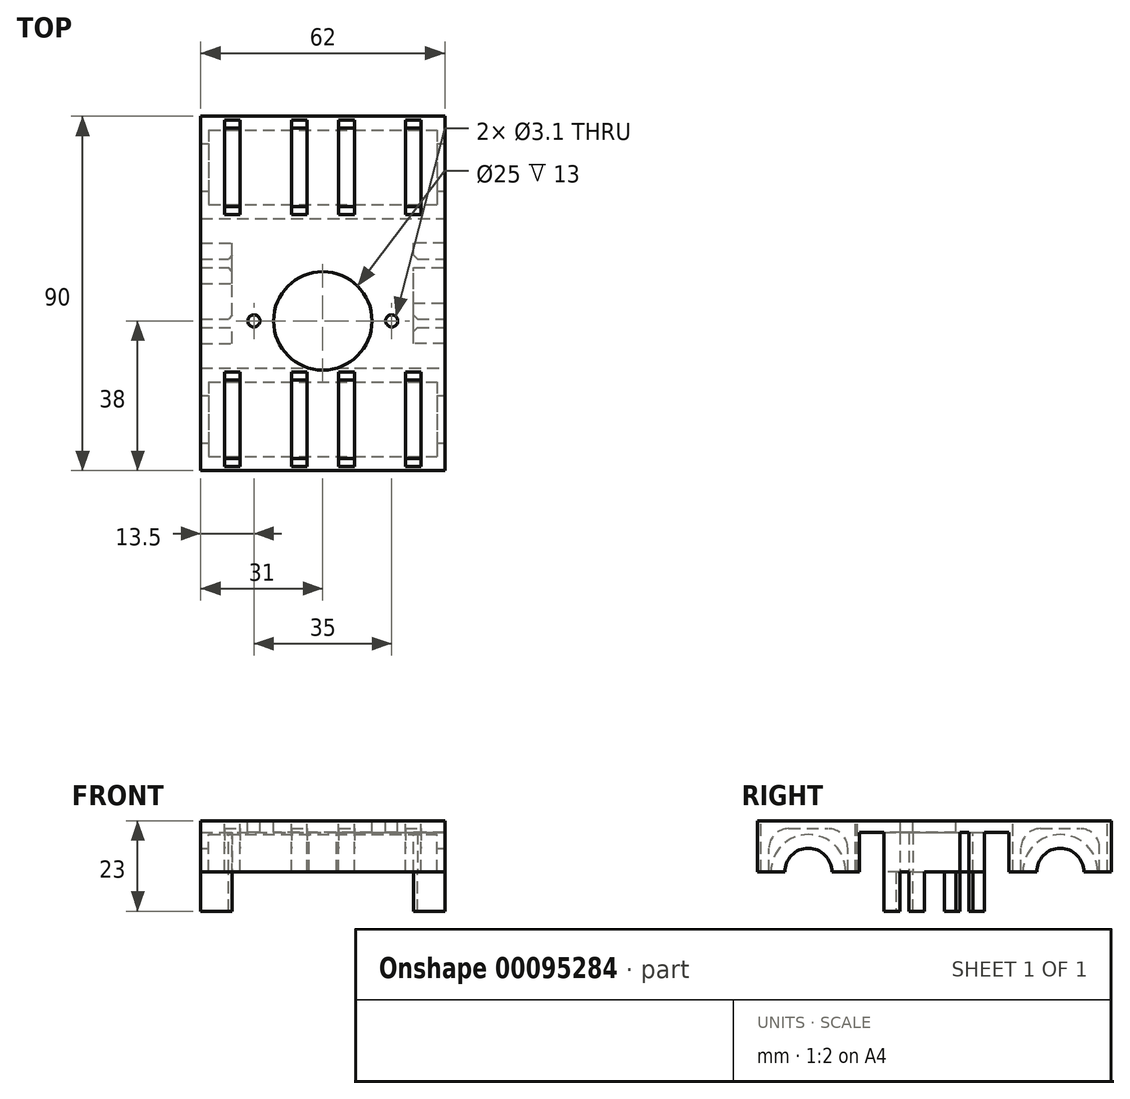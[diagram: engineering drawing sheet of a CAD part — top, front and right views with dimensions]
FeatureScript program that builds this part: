
annotation { "Feature Type Name" : "Feature", "Feature Type Description" : "" }
export const myFeature = defineFeature(function(context is Context, id is Id, definition is map)
    precondition{}
    {
        {
            var Q0;
            Q0=qCreatedBy(makeId("Top.planeOp"),FACE);
            var sketch = newSketch(context, id + "F0", { "sketchPlane" : qUnion([Q0])});
            skLineSegment(sketch, "E0.bottom", {"start": v(31, 45) * mm, "end": v(-31, 45) * mm});
            skLineSegment(sketch, "E0.top", {"start": v(31, -45) * mm, "end": v(-31, -45) * mm});
            skLineSegment(sketch, "E0.left", {"start": v(31, 45) * mm, "end": v(31, -45) * mm});
            skLineSegment(sketch, "E0.right", {"start": v(-31, 45) * mm, "end": v(-31, -45) * mm});
            skPoint(sketch, "E0.middle", {"position": v(0, 0) * mm});
            skLineSegment(sketch, "E1.bottom", {"start": v(-29, -22.5) * mm, "end": v(0, -22.5) * mm, "construction": true});
            skLineSegment(sketch, "E1.top", {"start": v(-29, -41.5) * mm, "end": v(0, -41.5) * mm, "construction": true});
            skLineSegment(sketch, "E1.left", {"start": v(-29, -22.5) * mm, "end": v(-29, -41.5) * mm, "construction": true});
            skLineSegment(sketch, "E1.right", {"start": v(0, -22.5) * mm, "end": v(0, -41.5) * mm});
            skLineSegment(sketch, "E2.bottom", {"start": v(0, -22.5) * mm, "end": v(29, -22.5) * mm, "construction": true});
            skLineSegment(sketch, "E2.top", {"start": v(0, -41.5) * mm, "end": v(29, -41.5) * mm, "construction": true});
            skLineSegment(sketch, "E2.left", {"start": v(0, -22.5) * mm, "end": v(0, -41.5) * mm, "construction": true});
            skLineSegment(sketch, "E2.right", {"start": v(29, -22.5) * mm, "end": v(29, -41.5) * mm, "construction": true});
            skLineSegment(sketch, "E3.MirrorCS", {"start": v(-29, 22.5) * mm, "end": v(0, 22.5) * mm, "construction": true});
            skLineSegment(sketch, "E4.MirrorCS", {"start": v(-29, 22.5) * mm, "end": v(-29, 41.5) * mm, "construction": true});
            skLineSegment(sketch, "E5.MirrorCS", {"start": v(-29, 41.5) * mm, "end": v(0, 41.5) * mm, "construction": true});
            skLineSegment(sketch, "E6.MirrorCS", {"start": v(0, 41.5) * mm, "end": v(29, 41.5) * mm, "construction": true});
            skLineSegment(sketch, "E7.MirrorCS", {"start": v(0, 22.5) * mm, "end": v(0, 41.5) * mm, "construction": true});
            skLineSegment(sketch, "E8.MirrorCS", {"start": v(0, 22.5) * mm, "end": v(29, 22.5) * mm, "construction": true});
            skLineSegment(sketch, "E9.MirrorCS", {"start": v(29, 22.5) * mm, "end": v(29, 41.5) * mm, "construction": true});
            skPoint(sketch, "E10", {"position": v(0, 32) * mm});
            skPoint(sketch, "E11", {"position": v(0, -32) * mm});
            skLineSegment(sketch, "E12.bottom", {"start": v(38, -27) * mm, "end": v(-38, -27) * mm, "construction": true});
            skLineSegment(sketch, "E12.top", {"start": v(38, -37) * mm, "end": v(-38, -37) * mm, "construction": true});
            skLineSegment(sketch, "E12.left", {"start": v(38, -27) * mm, "end": v(38, -37) * mm, "construction": true});
            skLineSegment(sketch, "E12.right", {"start": v(-38, -27) * mm, "end": v(-38, -37) * mm, "construction": true});
            skSolve(sketch);
        }
        {
            var Q0;
            Q0 = qSketchRegion(id + "F0", true);
            extrude(context, id + "F1", {"entities" : qUnion([Q0]), "depth" : 3 * mm});
        }
        {
            var Q0;
            Q0=makeQuery(id+"F1.opExtrude","CAP_FACE",FACE,{"disambiguationData":[OSD([sQuery(id+"F0.wireOp",EDGE,"E0.bottom"),sQuery(id+"F0.wireOp",EDGE,"E0.top"),sQuery(id+"F0.wireOp",EDGE,"E0.left"),sQuery(id+"F0.wireOp",EDGE,"E0.right"),sQuery(id+"F0.wireOp",EDGE,"JYYRxy27-rgmN-2rHz-wlqE-8sxhEuyDvCgZ"),sQuery(id+"F0.wireOp",EDGE,"MYyJY7mb-jWNP-WgpS-Wrbd-b0EtJ2tdOFdo"),sQuery(id+"F0.wireOp",EDGE,"f8288d83-7b8a-4c9c-ad61-19536bc560240.MirrorC")])],"isStart":true});
            var sketch = newSketch(context, id + "F2", { "sketchPlane" : qUnion([Q0])});
            skLineSegment(sketch, "E13.bottom", {"start": v(-31, 45) * mm, "end": v(31, 45) * mm});
            skLineSegment(sketch, "E13.top", {"start": v(-31, 19) * mm, "end": v(31, 19) * mm});
            skLineSegment(sketch, "E13.left", {"start": v(-31, 45) * mm, "end": v(-31, 19) * mm});
            skLineSegment(sketch, "E13.right", {"start": v(31, 45) * mm, "end": v(31, 19) * mm});
            skLineSegment(sketch, "E14", {"start": v(-31, 32) * mm, "end": v(31, 32) * mm, "construction": true});
            skLineSegment(sketch, "E15.MirrorCS", {"start": v(-31, -32) * mm, "end": v(31, -32) * mm, "construction": true});
            skLineSegment(sketch, "E16.MirrorCS", {"start": v(31, -45) * mm, "end": v(31, -19) * mm});
            skLineSegment(sketch, "E17.MirrorCS", {"start": v(-31, -45) * mm, "end": v(-31, -19) * mm});
            skLineSegment(sketch, "E18.MirrorCS", {"start": v(-31, -19) * mm, "end": v(31, -19) * mm});
            skLineSegment(sketch, "E19.MirrorCS", {"start": v(-31, -45) * mm, "end": v(31, -45) * mm});
            skSolve(sketch);
        }
        {
            var Q0;
            Q0 = qSketchRegion(id + "F2", true);
            extrude(context, id + "F3", {"entities" : qUnion([Q0]), "operationType" : NewBodyOperationType.ADD, "depth" : (20 / 2) * mm});
        }
        {
            var Q0;
            Q0=qCreatedBy(makeId("Right.planeOp"),FACE);
            var sketch = newSketch(context, id + "F4", { "sketchPlane" : qUnion([Q0])});
            skCircle(sketch, "E20", {"center": v(-32, -10) * mm, "radius": 9.5 * mm});
            skCircle(sketch, "E21.MirrorC", {"center": v(32, -10) * mm, "radius": 9.5 * mm});
            skSolve(sketch);
        }
        {
            var Q0;
            Q0 = qSketchRegion(id + "F4", true);
            var Q1;
            Q1=sQuery(id+"F4.wireOp",EDGE,"E20");
            extrude(context, id + "F5", {"entities" : qUnion([Q0]), "operationType" : NewBodyOperationType.REMOVE, "surfaceEntities" : qUnion([Q1]), "endBound" : BoundingType.SYMMETRIC, "oppositeDirection" : true, "depth" : (29 * 2) * mm});
        }
        {
            var Q0;
            Q0=qCreatedBy(makeId("Right.planeOp"),FACE);
            var sketch = newSketch(context, id + "F6", { "sketchPlane" : qUnion([Q0])});
            skCircle(sketch, "E22", {"center": v(-32, -10) * mm, "radius": 6 * mm});
            skCircle(sketch, "E23.MirrorC", {"center": v(32, -10) * mm, "radius": 6 * mm});
            skSolve(sketch);
        }
        {
            var Q0;
            Q0 = qSketchRegion(id + "F6", true);
            extrude(context, id + "F7", {"entities" : qUnion([Q0]), "operationType" : NewBodyOperationType.REMOVE, "endBound" : BoundingType.THROUGH_ALL, "oppositeDirection" : true, "depth" : 25 * mm, "hasSecondDirection" : true, "secondDirectionBound" : SecondDirectionBoundingType.THROUGH_ALL, "secondDirectionOppositeDirection" : false, "secondDirectionDepth" : 25 * mm});
        }
        {
            var Q0;
            Q0=makeQuery(id+"F1.opExtrude","CAP_FACE",FACE,{"disambiguationData":[OSD([sQuery(id+"F0.wireOp",EDGE,"E0.bottom"),sQuery(id+"F0.wireOp",EDGE,"E0.top"),sQuery(id+"F0.wireOp",EDGE,"E0.left"),sQuery(id+"F0.wireOp",EDGE,"E0.right"),sQuery(id+"F0.wireOp",EDGE,"MYyJY7mb-jWNP-WgpS-Wrbd-b0EtJ2tdOFdo"),sQuery(id+"F0.wireOp",EDGE,"f8288d83-7b8a-4c9c-ad61-19536bc560240.MirrorC")])],"isStart":false});
            var sketch = newSketch(context, id + "F8", { "sketchPlane" : qUnion([Q0])});
            skLineSegment(sketch, "E24.bottom", {"start": v(-29, -22.5) * mm, "end": v(0, -22.5) * mm, "construction": true});
            skLineSegment(sketch, "E24.top", {"start": v(-29, -41.5) * mm, "end": v(0, -41.5) * mm, "construction": true});
            skLineSegment(sketch, "E24.left", {"start": v(-29, -22.5) * mm, "end": v(-29, -41.5) * mm, "construction": true});
            skLineSegment(sketch, "E25.bottom", {"start": v(0, -22.5) * mm, "end": v(29, -22.5) * mm, "construction": true});
            skLineSegment(sketch, "E25.top", {"start": v(0, -41.5) * mm, "end": v(29, -41.5) * mm, "construction": true});
            skLineSegment(sketch, "E25.left", {"start": v(0, -22.5) * mm, "end": v(0, -41.5) * mm, "construction": true});
            skLineSegment(sketch, "E25.right", {"start": v(29, -22.5) * mm, "end": v(29, -41.5) * mm, "construction": true});
            skCircle(sketch, "E26", {"center": v(0, -7) * mm, "radius": 12.5 * mm});
            skCircle(sketch, "E27", {"center": v(-17.5, -7) * mm, "radius": 1.55 * mm});
            skPoint(sketch, "E28", {"position": v(0, -32) * mm});
            skCircle(sketch, "E29.MirrorC", {"center": v(17.5, -7) * mm, "radius": 1.55 * mm});
            skLineSegment(sketch, "E30", {"start": v(-38.23, -32) * mm, "end": v(52.87, -32) * mm, "construction": true});
            skLineSegment(sketch, "E31.MirrorCS", {"start": v(-29, 41.5) * mm, "end": v(0, 41.5) * mm, "construction": true});
            skLineSegment(sketch, "E32.MirrorCS", {"start": v(0, 41.5) * mm, "end": v(29, 41.5) * mm, "construction": true});
            skLineSegment(sketch, "E33.MirrorCS", {"start": v(29, 22.5) * mm, "end": v(29, 41.5) * mm, "construction": true});
            skLineSegment(sketch, "E34.MirrorCS", {"start": v(0, 22.5) * mm, "end": v(29, 22.5) * mm, "construction": true});
            skLineSegment(sketch, "E35.MirrorCS", {"start": v(0, 22.5) * mm, "end": v(0, 41.5) * mm, "construction": true});
            skLineSegment(sketch, "E36.MirrorCS", {"start": v(-38.23, 32) * mm, "end": v(52.87, 32) * mm, "construction": true});
            skLineSegment(sketch, "E37.MirrorCS", {"start": v(-29, 22.5) * mm, "end": v(0, 22.5) * mm, "construction": true});
            skLineSegment(sketch, "E38.MirrorCS", {"start": v(-29, 22.5) * mm, "end": v(-29, 41.5) * mm, "construction": true});
            skSolve(sketch);
        }
        {
            var Q0;
            Q0 = qSketchRegion(id + "F8", true);
            extrude(context, id + "F9", {"entities" : qUnion([Q0]), "operationType" : NewBodyOperationType.REMOVE, "endBound" : BoundingType.THROUGH_ALL, "oppositeDirection" : true, "depth" : 25 * mm});
        }
        {
            var Q0;
            Q0=qCreatedBy(makeId("Right.planeOp"),FACE);
            cPlane(context, id + "F10", {"entities" : qUnion([Q0]), "cplaneType" : CPlaneType.OFFSET, "offset" : (29 - 6) * mm, "width" : 150 * mm, "height" : 150 * mm});
        }
        {
            var Q0;
            Q0=qCreatedBy(id+"F10.planeOp",FACE);
            var sketch = newSketch(context, id + "F11", { "sketchPlane" : qUnion([Q0])});
            skLineSegment(sketch, "E39.bottom", {"start": v(-44, -10) * mm, "end": v(-42, -10) * mm});
            skLineSegment(sketch, "E39.top", {"start": v(-44, 3) * mm, "end": v(-20, 3) * mm});
            skLineSegment(sketch, "E39.left", {"start": v(-44, -10) * mm, "end": v(-44, 3) * mm});
            skLineSegment(sketch, "E39.right", {"start": v(-20, -10) * mm, "end": v(-20, 3) * mm});
            skLineSegment(sketch, "E40.top", {"start": v(-37, 1) * mm, "end": v(-27, 1) * mm});
            skLineSegment(sketch, "E40.left", {"start": v(-42, -10) * mm, "end": v(-42, -4) * mm});
            skLineSegment(sketch, "E40.right", {"start": v(-22, -10) * mm, "end": v(-22, -4) * mm});
            skLineSegment(sketch, "E41.trimOffspring", {"start": v(-22, -10) * mm, "end": v(-20, -10) * mm});
            skPoint(sketch, "E42.visualSharp", {"position": v(-42, 1) * mm});
            skArc(sketch, "E42.filletArc", {"start": v(-37, 1) * mm, "mid": v(-40.54, -0.46) * mm, "end": v(-42, -4) * mm});
            skPoint(sketch, "E43.visualSharp", {"position": v(-22, 1) * mm});
            skArc(sketch, "E43.filletArc", {"start": v(-22, -4) * mm, "mid": v(-23.46, -0.46) * mm, "end": v(-27, 1) * mm});
            skLineSegment(sketch, "E44", {"start": v(-32, -18.67) * mm, "end": v(-32, 4.8) * mm, "construction": true});
            skPoint(sketch, "E45", {"position": v(-32, -10) * mm});
            skPoint(sketch, "E46", {"position": v(-32, 1) * mm});
            skLineSegment(sketch, "E47.MirrorCS", {"start": v(-20, -10) * mm, "end": v(-22, -10) * mm});
            skLineSegment(sketch, "E48.MirrorCS", {"start": v(-20, 3) * mm, "end": v(-44, 3) * mm});
            skArc(sketch, "E49.MirrorCS", {"start": v(-27, 1) * mm, "mid": v(-23.46, -0.46) * mm, "end": v(-22, -4) * mm});
            skArc(sketch, "E50.MirrorCS", {"start": v(-42, -4) * mm, "mid": v(-40.54, -0.46) * mm, "end": v(-37, 1) * mm});
            skLineSegment(sketch, "E51.MirrorCS", {"start": v(-42, -10) * mm, "end": v(-44, -10) * mm});
            skLineSegment(sketch, "E52.MirrorCS", {"start": v(-27, 1) * mm, "end": v(-37, 1) * mm});
            skPoint(sketch, "E53.MirrorP", {"position": v(32, -10) * mm});
            skPoint(sketch, "E54.MirrorP", {"position": v(22, 1) * mm});
            skLineSegment(sketch, "E55.MirrorCS", {"start": v(42, -10) * mm, "end": v(42, -4) * mm});
            skLineSegment(sketch, "E56.MirrorCS", {"start": v(20, -10) * mm, "end": v(20, 3) * mm});
            skLineSegment(sketch, "E57.MirrorCS", {"start": v(44, -10) * mm, "end": v(44, 3) * mm});
            skLineSegment(sketch, "E58.MirrorCS", {"start": v(37, 1) * mm, "end": v(27, 1) * mm});
            skLineSegment(sketch, "E59.MirrorCS", {"start": v(42, -10) * mm, "end": v(44, -10) * mm});
            skLineSegment(sketch, "E60.MirrorCS", {"start": v(22, -10) * mm, "end": v(22, -4) * mm});
            skArc(sketch, "E61.MirrorCS", {"start": v(27, 1) * mm, "mid": v(23.46, -0.46) * mm, "end": v(22, -4) * mm});
            skArc(sketch, "E62.MirrorCS", {"start": v(37, 1) * mm, "mid": v(40.54, -0.46) * mm, "end": v(42, -4) * mm});
            skLineSegment(sketch, "E63.MirrorCS", {"start": v(20, 3) * mm, "end": v(44, 3) * mm});
            skLineSegment(sketch, "E64.MirrorCS", {"start": v(20, -10) * mm, "end": v(22, -10) * mm});
            skPoint(sketch, "E65.MirrorP", {"position": v(42, 1) * mm});
            skPoint(sketch, "E66.MirrorP", {"position": v(32, 1) * mm});
            skArc(sketch, "E67.MirrorCS", {"start": v(42, -4) * mm, "mid": v(40.54, -0.46) * mm, "end": v(37, 1) * mm});
            skArc(sketch, "E68.MirrorCS", {"start": v(22, -4) * mm, "mid": v(23.46, -0.46) * mm, "end": v(27, 1) * mm});
            skLineSegment(sketch, "E69.MirrorCS", {"start": v(44, 3) * mm, "end": v(20, 3) * mm});
            skLineSegment(sketch, "E70.MirrorCS", {"start": v(44, -10) * mm, "end": v(42, -10) * mm});
            skLineSegment(sketch, "E71.MirrorCS", {"start": v(32, -18.67) * mm, "end": v(32, 4.8) * mm, "construction": true});
            skLineSegment(sketch, "E72.MirrorCS", {"start": v(27, 1) * mm, "end": v(37, 1) * mm});
            skLineSegment(sketch, "E73.MirrorCS", {"start": v(22, -10) * mm, "end": v(20, -10) * mm});
            skSolve(sketch);
        }
        {
            var Q0;
            Q0=qCreatedBy(makeId("Right.planeOp"),FACE);
            cPlane(context, id + "F12", {"entities" : qUnion([Q0]), "cplaneType" : CPlaneType.OFFSET, "offset" : 6 * mm, "width" : 150 * mm, "height" : 150 * mm});
        }
        {
            var Q0;
            Q0=qCreatedBy(id+"F12.planeOp",FACE);
            var sketch = newSketch(context, id + "F13", { "sketchPlane" : qUnion([Q0])});
            skLineSegment(sketch, "E74.bottom", {"start": v(-44, -10) * mm, "end": v(-42, -10) * mm});
            skLineSegment(sketch, "E74.top", {"start": v(-44, 3) * mm, "end": v(-20, 3) * mm});
            skLineSegment(sketch, "E74.left", {"start": v(-44, -10) * mm, "end": v(-44, 3) * mm});
            skLineSegment(sketch, "E74.right", {"start": v(-20, -10) * mm, "end": v(-20, 3) * mm});
            skLineSegment(sketch, "E75.top", {"start": v(-37, 1) * mm, "end": v(-27, 1) * mm});
            skLineSegment(sketch, "E75.left", {"start": v(-42, -10) * mm, "end": v(-42, -4) * mm});
            skLineSegment(sketch, "E75.right", {"start": v(-22, -10) * mm, "end": v(-22, -4) * mm});
            skLineSegment(sketch, "E76.trimOffspring", {"start": v(-22, -10) * mm, "end": v(-20, -10) * mm});
            skPoint(sketch, "E77.visualSharp", {"position": v(-42, 1) * mm});
            skArc(sketch, "E77.filletArc", {"start": v(-37, 1) * mm, "mid": v(-40.54, -0.46) * mm, "end": v(-42, -4) * mm});
            skPoint(sketch, "E78.visualSharp", {"position": v(-22, 1) * mm});
            skArc(sketch, "E78.filletArc", {"start": v(-22, -4) * mm, "mid": v(-23.46, -0.46) * mm, "end": v(-27, 1) * mm});
            skLineSegment(sketch, "E79", {"start": v(-32, -15.28) * mm, "end": v(-32, 8.2) * mm, "construction": true});
            skPoint(sketch, "E80", {"position": v(-32, -10) * mm});
            skPoint(sketch, "E81", {"position": v(-32, 1) * mm});
            skLineSegment(sketch, "E82.MirrorCS", {"start": v(-20, -10) * mm, "end": v(-22, -10) * mm});
            skLineSegment(sketch, "E83.MirrorCS", {"start": v(-20, 3) * mm, "end": v(-44, 3) * mm});
            skArc(sketch, "E84.MirrorCS", {"start": v(-27, 1) * mm, "mid": v(-23.46, -0.46) * mm, "end": v(-22, -4) * mm});
            skArc(sketch, "E85.MirrorCS", {"start": v(-42, -4) * mm, "mid": v(-40.54, -0.46) * mm, "end": v(-37, 1) * mm});
            skLineSegment(sketch, "E86.MirrorCS", {"start": v(-42, -10) * mm, "end": v(-44, -10) * mm});
            skLineSegment(sketch, "E87.MirrorCS", {"start": v(-27, 1) * mm, "end": v(-37, 1) * mm});
            skLineSegment(sketch, "E88.MirrorCS", {"start": v(22, -10) * mm, "end": v(20, -10) * mm});
            skLineSegment(sketch, "E89.MirrorCS", {"start": v(44, -10) * mm, "end": v(42, -10) * mm});
            skPoint(sketch, "E90.MirrorP", {"position": v(32, -10) * mm});
            skLineSegment(sketch, "E91.MirrorCS", {"start": v(20, -10) * mm, "end": v(20, 3) * mm});
            skLineSegment(sketch, "E92.MirrorCS", {"start": v(44, -10) * mm, "end": v(44, 3) * mm});
            skArc(sketch, "E93.MirrorCS", {"start": v(37, 1) * mm, "mid": v(40.54, -0.46) * mm, "end": v(42, -4) * mm});
            skLineSegment(sketch, "E94.MirrorCS", {"start": v(44, 3) * mm, "end": v(20, 3) * mm});
            skPoint(sketch, "E95.MirrorP", {"position": v(22, 1) * mm});
            skLineSegment(sketch, "E96.MirrorCS", {"start": v(42, -10) * mm, "end": v(42, -4) * mm});
            skLineSegment(sketch, "E97.MirrorCS", {"start": v(37, 1) * mm, "end": v(27, 1) * mm});
            skPoint(sketch, "E98.MirrorP", {"position": v(32, 1) * mm});
            skLineSegment(sketch, "E99.MirrorCS", {"start": v(22, -10) * mm, "end": v(22, -4) * mm});
            skArc(sketch, "E100.MirrorCS", {"start": v(27, 1) * mm, "mid": v(23.46, -0.46) * mm, "end": v(22, -4) * mm});
            skPoint(sketch, "E101.MirrorP", {"position": v(42, 1) * mm});
            skLineSegment(sketch, "E102.MirrorCS", {"start": v(42, -10) * mm, "end": v(44, -10) * mm});
            skLineSegment(sketch, "E103.MirrorCS", {"start": v(20, 3) * mm, "end": v(44, 3) * mm});
            skArc(sketch, "E104.MirrorCS", {"start": v(22, -4) * mm, "mid": v(23.46, -0.46) * mm, "end": v(27, 1) * mm});
            skArc(sketch, "E105.MirrorCS", {"start": v(42, -4) * mm, "mid": v(40.54, -0.46) * mm, "end": v(37, 1) * mm});
            skLineSegment(sketch, "E106.MirrorCS", {"start": v(27, 1) * mm, "end": v(37, 1) * mm});
            skLineSegment(sketch, "E107.MirrorCS", {"start": v(20, -10) * mm, "end": v(22, -10) * mm});
            skLineSegment(sketch, "E108.MirrorCS", {"start": v(32, -15.28) * mm, "end": v(32, 8.2) * mm, "construction": true});
            skSolve(sketch);
        }
        {
            var Q0;
            Q0=qCreatedBy(makeId("Right.planeOp"),FACE);
            cPlane(context, id + "F14", {"entities" : qUnion([Q0]), "cplaneType" : CPlaneType.OFFSET, "offset" : (29 - 6) * mm, "oppositeDirection" : true, "width" : 150 * mm, "height" : 150 * mm});
        }
        {
            var Q0;
            Q0=qCreatedBy(id+"F14.planeOp",FACE);
            var sketch = newSketch(context, id + "F15", { "sketchPlane" : qUnion([Q0])});
            skLineSegment(sketch, "E109.bottom", {"start": v(-44, -10) * mm, "end": v(-42, -10) * mm});
            skLineSegment(sketch, "E109.top", {"start": v(-44, 3) * mm, "end": v(-20, 3) * mm});
            skLineSegment(sketch, "E109.left", {"start": v(-44, -10) * mm, "end": v(-44, 3) * mm});
            skLineSegment(sketch, "E109.right", {"start": v(-20, -10) * mm, "end": v(-20, 3) * mm});
            skLineSegment(sketch, "E110.top", {"start": v(-37, 1) * mm, "end": v(-27, 1) * mm});
            skLineSegment(sketch, "E110.left", {"start": v(-42, -10) * mm, "end": v(-42, -4) * mm});
            skLineSegment(sketch, "E110.right", {"start": v(-22, -10) * mm, "end": v(-22, -4) * mm});
            skLineSegment(sketch, "E111.trimOffspring", {"start": v(-22, -10) * mm, "end": v(-20, -10) * mm});
            skPoint(sketch, "E112.visualSharp", {"position": v(-42, 1) * mm});
            skArc(sketch, "E112.filletArc", {"start": v(-37, 1) * mm, "mid": v(-40.54, -0.46) * mm, "end": v(-42, -4) * mm});
            skPoint(sketch, "E113.visualSharp", {"position": v(-22, 1) * mm});
            skArc(sketch, "E113.filletArc", {"start": v(-22, -4) * mm, "mid": v(-23.46, -0.46) * mm, "end": v(-27, 1) * mm});
            skLineSegment(sketch, "E114", {"start": v(-32, -15.28) * mm, "end": v(-32, 8.2) * mm, "construction": true});
            skPoint(sketch, "E115", {"position": v(-32, -10) * mm});
            skPoint(sketch, "E116", {"position": v(-32, 1) * mm});
            skLineSegment(sketch, "E117.MirrorCS", {"start": v(-20, -10) * mm, "end": v(-22, -10) * mm});
            skLineSegment(sketch, "E118.MirrorCS", {"start": v(-20, 3) * mm, "end": v(-44, 3) * mm});
            skArc(sketch, "E119.MirrorCS", {"start": v(-27, 1) * mm, "mid": v(-23.46, -0.46) * mm, "end": v(-22, -4) * mm});
            skArc(sketch, "E120.MirrorCS", {"start": v(-42, -4) * mm, "mid": v(-40.54, -0.46) * mm, "end": v(-37, 1) * mm});
            skLineSegment(sketch, "E121.MirrorCS", {"start": v(-42, -10) * mm, "end": v(-44, -10) * mm});
            skLineSegment(sketch, "E122.MirrorCS", {"start": v(-27, 1) * mm, "end": v(-37, 1) * mm});
            skLineSegment(sketch, "E123.MirrorCS", {"start": v(44, -10) * mm, "end": v(42, -10) * mm});
            skLineSegment(sketch, "E124.MirrorCS", {"start": v(22, -10) * mm, "end": v(22, -4) * mm});
            skLineSegment(sketch, "E125.MirrorCS", {"start": v(44, -10) * mm, "end": v(44, 3) * mm});
            skLineSegment(sketch, "E126.MirrorCS", {"start": v(20, -10) * mm, "end": v(22, -10) * mm});
            skArc(sketch, "E127.MirrorCS", {"start": v(27, 1) * mm, "mid": v(23.46, -0.46) * mm, "end": v(22, -4) * mm});
            skPoint(sketch, "E128.MirrorP", {"position": v(32, 1) * mm});
            skLineSegment(sketch, "E129.MirrorCS", {"start": v(20, -10) * mm, "end": v(20, 3) * mm});
            skPoint(sketch, "E130.MirrorP", {"position": v(42, 1) * mm});
            skLineSegment(sketch, "E131.MirrorCS", {"start": v(27, 1) * mm, "end": v(37, 1) * mm});
            skPoint(sketch, "E132.MirrorP", {"position": v(32, -10) * mm});
            skArc(sketch, "E133.MirrorCS", {"start": v(37, 1) * mm, "mid": v(40.54, -0.46) * mm, "end": v(42, -4) * mm});
            skLineSegment(sketch, "E134.MirrorCS", {"start": v(42, -10) * mm, "end": v(42, -4) * mm});
            skLineSegment(sketch, "E135.MirrorCS", {"start": v(20, 3) * mm, "end": v(44, 3) * mm});
            skPoint(sketch, "E136.MirrorP", {"position": v(22, 1) * mm});
            skLineSegment(sketch, "E137.MirrorCS", {"start": v(37, 1) * mm, "end": v(27, 1) * mm});
            skLineSegment(sketch, "E138.MirrorCS", {"start": v(22, -10) * mm, "end": v(20, -10) * mm});
            skLineSegment(sketch, "E139.MirrorCS", {"start": v(32, -15.28) * mm, "end": v(32, 8.2) * mm, "construction": true});
            skLineSegment(sketch, "E140.MirrorCS", {"start": v(44, 3) * mm, "end": v(20, 3) * mm});
            skArc(sketch, "E141.MirrorCS", {"start": v(22, -4) * mm, "mid": v(23.46, -0.46) * mm, "end": v(27, 1) * mm});
            skArc(sketch, "E142.MirrorCS", {"start": v(42, -4) * mm, "mid": v(40.54, -0.46) * mm, "end": v(37, 1) * mm});
            skLineSegment(sketch, "E143.MirrorCS", {"start": v(42, -10) * mm, "end": v(44, -10) * mm});
            skSolve(sketch);
        }
        {
            var Q0;
            Q0=qCreatedBy(makeId("Right.planeOp"),FACE);
            cPlane(context, id + "F16", {"entities" : qUnion([Q0]), "cplaneType" : CPlaneType.OFFSET, "offset" : 6 * mm, "oppositeDirection" : true, "width" : 150 * mm, "height" : 150 * mm});
        }
        {
            var Q0;
            Q0=qCreatedBy(id+"F16.planeOp",FACE);
            var sketch = newSketch(context, id + "F17", { "sketchPlane" : qUnion([Q0])});
            skLineSegment(sketch, "E144.bottom", {"start": v(-44, -10) * mm, "end": v(-42, -10) * mm});
            skLineSegment(sketch, "E144.top", {"start": v(-44, 3) * mm, "end": v(-20, 3) * mm});
            skLineSegment(sketch, "E144.left", {"start": v(-44, -10) * mm, "end": v(-44, 3) * mm});
            skLineSegment(sketch, "E144.right", {"start": v(-20, -10) * mm, "end": v(-20, 3) * mm});
            skLineSegment(sketch, "E145.top", {"start": v(-37, 1) * mm, "end": v(-27, 1) * mm});
            skLineSegment(sketch, "E145.left", {"start": v(-42, -10) * mm, "end": v(-42, -4) * mm});
            skLineSegment(sketch, "E145.right", {"start": v(-22, -10) * mm, "end": v(-22, -4) * mm});
            skLineSegment(sketch, "E146.trimOffspring", {"start": v(-22, -10) * mm, "end": v(-20, -10) * mm});
            skPoint(sketch, "E147.visualSharp", {"position": v(-42, 1) * mm});
            skArc(sketch, "E147.filletArc", {"start": v(-37, 1) * mm, "mid": v(-40.54, -0.46) * mm, "end": v(-42, -4) * mm});
            skPoint(sketch, "E148.visualSharp", {"position": v(-22, 1) * mm});
            skArc(sketch, "E148.filletArc", {"start": v(-22, -4) * mm, "mid": v(-23.46, -0.46) * mm, "end": v(-27, 1) * mm});
            skLineSegment(sketch, "E149", {"start": v(-32, -15.28) * mm, "end": v(-32, 8.2) * mm, "construction": true});
            skPoint(sketch, "E150", {"position": v(-32, -10) * mm});
            skPoint(sketch, "E151", {"position": v(-32, 1) * mm});
            skLineSegment(sketch, "E152.MirrorCS", {"start": v(-20, -10) * mm, "end": v(-22, -10) * mm});
            skLineSegment(sketch, "E153.MirrorCS", {"start": v(-20, 3) * mm, "end": v(-44, 3) * mm});
            skArc(sketch, "E154.MirrorCS", {"start": v(-27, 1) * mm, "mid": v(-23.46, -0.46) * mm, "end": v(-22, -4) * mm});
            skArc(sketch, "E155.MirrorCS", {"start": v(-42, -4) * mm, "mid": v(-40.54, -0.46) * mm, "end": v(-37, 1) * mm});
            skLineSegment(sketch, "E156.MirrorCS", {"start": v(-42, -10) * mm, "end": v(-44, -10) * mm});
            skLineSegment(sketch, "E157.MirrorCS", {"start": v(-27, 1) * mm, "end": v(-37, 1) * mm});
            skPoint(sketch, "E158.MirrorP", {"position": v(22, 1) * mm});
            skLineSegment(sketch, "E159.MirrorCS", {"start": v(42, -10) * mm, "end": v(42, -4) * mm});
            skLineSegment(sketch, "E160.MirrorCS", {"start": v(20, -10) * mm, "end": v(22, -10) * mm});
            skLineSegment(sketch, "E161.MirrorCS", {"start": v(20, 3) * mm, "end": v(44, 3) * mm});
            skArc(sketch, "E162.MirrorCS", {"start": v(27, 1) * mm, "mid": v(23.46, -0.46) * mm, "end": v(22, -4) * mm});
            skPoint(sketch, "E163.MirrorP", {"position": v(32, 1) * mm});
            skArc(sketch, "E164.MirrorCS", {"start": v(42, -4) * mm, "mid": v(40.54, -0.46) * mm, "end": v(37, 1) * mm});
            skLineSegment(sketch, "E165.MirrorCS", {"start": v(20, -10) * mm, "end": v(20, 3) * mm});
            skLineSegment(sketch, "E166.MirrorCS", {"start": v(27, 1) * mm, "end": v(37, 1) * mm});
            skPoint(sketch, "E167.MirrorP", {"position": v(32, -10) * mm});
            skPoint(sketch, "E168.MirrorP", {"position": v(42, 1) * mm});
            skLineSegment(sketch, "E169.MirrorCS", {"start": v(44, -10) * mm, "end": v(44, 3) * mm});
            skLineSegment(sketch, "E170.MirrorCS", {"start": v(22, -10) * mm, "end": v(22, -4) * mm});
            skLineSegment(sketch, "E171.MirrorCS", {"start": v(42, -10) * mm, "end": v(44, -10) * mm});
            skLineSegment(sketch, "E172.MirrorCS", {"start": v(32, -15.28) * mm, "end": v(32, 8.2) * mm, "construction": true});
            skLineSegment(sketch, "E173.MirrorCS", {"start": v(44, -10) * mm, "end": v(42, -10) * mm});
            skArc(sketch, "E174.MirrorCS", {"start": v(37, 1) * mm, "mid": v(40.54, -0.46) * mm, "end": v(42, -4) * mm});
            skArc(sketch, "E175.MirrorCS", {"start": v(22, -4) * mm, "mid": v(23.46, -0.46) * mm, "end": v(27, 1) * mm});
            skLineSegment(sketch, "E176.MirrorCS", {"start": v(22, -10) * mm, "end": v(20, -10) * mm});
            skLineSegment(sketch, "E177.MirrorCS", {"start": v(37, 1) * mm, "end": v(27, 1) * mm});
            skLineSegment(sketch, "E178.MirrorCS", {"start": v(44, 3) * mm, "end": v(20, 3) * mm});
            skSolve(sketch);
        }
        {
            var Q0;
            Q0 = qSketchRegion(id + "F11", true);
            var Q1;
            Q1 = qSketchRegion(id + "F13", true);
            var Q2;
            Q2 = qSketchRegion(id + "F15", true);
            var Q3;
            Q3 = qSketchRegion(id + "F17", true);
            extrude(context, id + "F18", {"entities" : qUnion([Q0, Q1, Q2, Q3]), "operationType" : NewBodyOperationType.REMOVE, "endBound" : BoundingType.SYMMETRIC, "oppositeDirection" : true, "depth" : 4 * mm});
        }
        {
            var Q0;
            Q0=makeQuery(id+"F1.opExtrude","CAP_FACE",FACE,{"disambiguationData":[OSD([sQuery(id+"F0.wireOp",EDGE,"E0.bottom"),sQuery(id+"F0.wireOp",EDGE,"E0.top"),sQuery(id+"F0.wireOp",EDGE,"E0.left"),sQuery(id+"F0.wireOp",EDGE,"E0.right")])],"isStart":true});
            var sketch = newSketch(context, id + "F19", { "sketchPlane" : qUnion([Q0])});
            skLineSegment(sketch, "E179.bottom", {"start": v(31, 12.75) * mm, "end": v(23, 12.75) * mm});
            skLineSegment(sketch, "E179.top", {"start": v(31, -12.75) * mm, "end": v(23, -12.75) * mm});
            skLineSegment(sketch, "E179.left", {"start": v(31, 12.75) * mm, "end": v(31, -12.75) * mm});
            skLineSegment(sketch, "E179.right", {"start": v(23, 12.75) * mm, "end": v(23, -12.75) * mm});
            skPoint(sketch, "E179.middle", {"position": v(27, 0) * mm});
            skPoint(sketch, "E180.MirrorP", {"position": v(-27, 0) * mm});
            skLineSegment(sketch, "E181.MirrorCS", {"start": v(-31, 12.75) * mm, "end": v(-31, -12.75) * mm});
            skLineSegment(sketch, "E182.MirrorCS", {"start": v(-31, -12.75) * mm, "end": v(-23, -12.75) * mm});
            skLineSegment(sketch, "E183.MirrorCS", {"start": v(-31, 12.75) * mm, "end": v(-23, 12.75) * mm});
            skLineSegment(sketch, "E184.MirrorCS", {"start": v(-23, 12.75) * mm, "end": v(-23, -12.75) * mm});
            skSolve(sketch);
        }
        {
            var Q0;
            Q0 = qSketchRegion(id + "F19", true);
            extrude(context, id + "F20", {"entities" : qUnion([Q0]), "operationType" : NewBodyOperationType.ADD, "depth" : 10 * mm});
        }
        {
            var Q0;
            Q0=makeQuery(id+"F20.opExtrude","CAP_FACE",FACE,{"disambiguationData":[OSD([sQuery(id+"F19.wireOp",EDGE,"E181.MirrorCS"),sQuery(id+"F19.wireOp",EDGE,"E182.MirrorCS"),sQuery(id+"F19.wireOp",EDGE,"E183.MirrorCS"),sQuery(id+"F19.wireOp",EDGE,"E184.MirrorCS")])],"isStart":false});
            var sketch = newSketch(context, id + "F21", { "sketchPlane" : qUnion([Q0])});
            skLineSegment(sketch, "E185.bottom", {"start": v(-31, 8.75) * mm, "end": v(-23, 8.75) * mm});
            skLineSegment(sketch, "E185.top", {"start": v(-31, 6.5) * mm, "end": v(-23, 6.5) * mm});
            skLineSegment(sketch, "E185.left", {"start": v(-31, 8.75) * mm, "end": v(-31, 6.5) * mm});
            skLineSegment(sketch, "E185.right", {"start": v(-23, 8.75) * mm, "end": v(-23, 6.5) * mm});
            skLineSegment(sketch, "E186.bottom", {"start": v(23, -6.5) * mm, "end": v(31, -6.5) * mm});
            skLineSegment(sketch, "E186.top", {"start": v(23, -8.75) * mm, "end": v(31, -8.75) * mm});
            skLineSegment(sketch, "E186.left", {"start": v(23, -6.5) * mm, "end": v(23, -8.75) * mm});
            skLineSegment(sketch, "E186.right", {"start": v(31, -6.5) * mm, "end": v(31, -8.75) * mm});
            skSolve(sketch);
        }
        {
            var Q0;
            Q0 = qSketchRegion(id + "F21", true);
            var Q1;
            Q1=makeQuery(id+"F1.opExtrude","CAP_FACE",FACE,{"disambiguationData":[OSD([sQuery(id+"F0.wireOp",EDGE,"E0.bottom"),sQuery(id+"F0.wireOp",EDGE,"E0.top"),sQuery(id+"F0.wireOp",EDGE,"E0.left"),sQuery(id+"F0.wireOp",EDGE,"E0.right")])],"isStart":true});
            extrude(context, id + "F22", {"entities" : qUnion([Q0]), "operationType" : NewBodyOperationType.REMOVE, "endBound" : BoundingType.UP_TO_SURFACE, "oppositeDirection" : true, "endBoundEntityFace" : qUnion([Q1]), "depth" : 25 * mm});
        }
        {
            var Q0;
            {var subQ0=sQuery(id+"F19.wireOp",EDGE,"E181.MirrorCS");var subQ1=sQuery(id+"F19.wireOp",EDGE,"E182.MirrorCS");var subQ2=sQuery(id+"F19.wireOp",EDGE,"E184.MirrorCS");Q0=makeQuery(id+"F22.boolean.opBoolean","SPLIT",FACE,{"disambiguationData":[TD([makeQuery(id+"F20.opExtrude","SWEPT_FACE",FACE,{"disambiguationData":[OSD([subQ1])]})])],"derivedFrom":makeQuery(id+"F20.opExtrude","CAP_FACE",FACE,{"disambiguationData":[OSD([subQ0,subQ1,sQuery(id+"F19.wireOp",EDGE,"E183.MirrorCS"),subQ2])],"isStart":false})});}
            var sketch = newSketch(context, id + "F23", { "sketchPlane" : qUnion([Q0])});
            skLineSegment(sketch, "E187.bottom", {"start": v(-31, -12.75) * mm, "end": v(-23, -12.75) * mm});
            skLineSegment(sketch, "E187.top", {"start": v(-31, -8.75) * mm, "end": v(-23, -8.75) * mm});
            skLineSegment(sketch, "E187.left", {"start": v(-31, -12.75) * mm, "end": v(-31, -8.75) * mm});
            skLineSegment(sketch, "E187.right", {"start": v(-23, -12.75) * mm, "end": v(-23, -8.75) * mm});
            skLineSegment(sketch, "E188.bottom", {"start": v(23, 12.75) * mm, "end": v(31, 12.75) * mm});
            skLineSegment(sketch, "E188.top", {"start": v(23, 8.75) * mm, "end": v(31, 8.75) * mm});
            skLineSegment(sketch, "E188.left", {"start": v(23, 12.75) * mm, "end": v(23, 8.75) * mm});
            skLineSegment(sketch, "E188.right", {"start": v(31, 12.75) * mm, "end": v(31, 8.75) * mm});
            skLineSegment(sketch, "E189.bottom", {"start": v(-31, -6.5) * mm, "end": v(-23, -6.5) * mm});
            skLineSegment(sketch, "E189.top", {"start": v(-31, -2.5) * mm, "end": v(-23, -2.5) * mm});
            skLineSegment(sketch, "E189.left", {"start": v(-31, -6.5) * mm, "end": v(-31, -2.5) * mm});
            skLineSegment(sketch, "E189.right", {"start": v(-23, -6.5) * mm, "end": v(-23, -2.5) * mm});
            skLineSegment(sketch, "E190.bottom", {"start": v(23, 6.5) * mm, "end": v(31, 6.5) * mm});
            skLineSegment(sketch, "E190.top", {"start": v(23, 2.5) * mm, "end": v(31, 2.5) * mm});
            skLineSegment(sketch, "E190.left", {"start": v(23, 6.5) * mm, "end": v(23, 2.5) * mm});
            skLineSegment(sketch, "E190.right", {"start": v(31, 6.5) * mm, "end": v(31, 2.5) * mm});
            skSolve(sketch);
        }
        {
            var Q0;
            Q0 = qSketchRegion(id + "F23", true);
            extrude(context, id + "F24", {"entities" : qUnion([Q0]), "operationType" : NewBodyOperationType.ADD, "depth" : 10 * mm});
        }
        {
            var Q0;
            Q0=makeQuery(id+"F22.boolean.opBoolean","COPY",EDGE,{"derivedFrom":makeQuery(id+"F22.opExtrude","SWEPT_EDGE",EDGE,{"disambiguationData":[OSD([sQuery(id+"F19.wireOp",EDGE,"E184.MirrorCS"),sQuery(id+"F21.wireOp",EDGE,"E185.bottom"),sQuery(id+"F21.wireOp",EDGE,"E185.right")])]})});
            var Q1;
            Q1=makeQuery(id+"F22.boolean.opBoolean","COPY",EDGE,{"derivedFrom":makeQuery(id+"F22.opExtrude","SWEPT_EDGE",EDGE,{"disambiguationData":[OSD([sQuery(id+"F19.wireOp",EDGE,"E184.MirrorCS"),sQuery(id+"F21.wireOp",EDGE,"E185.top"),sQuery(id+"F21.wireOp",EDGE,"E185.right")])]})});
            var Q2;
            Q2=makeQuery(id+"F24.opExtrude","SWEPT_EDGE",EDGE,{"disambiguationData":[OSD([sQuery(id+"F19.wireOp",EDGE,"E184.MirrorCS"),sQuery(id+"F23.wireOp",EDGE,"E189.bottom"),sQuery(id+"F23.wireOp",EDGE,"E189.right")])]});
            var Q3;
            Q3=makeQuery(id+"F24.opExtrude","SWEPT_EDGE",EDGE,{"disambiguationData":[OSD([sQuery(id+"F19.wireOp",EDGE,"E184.MirrorCS"),sQuery(id+"F23.wireOp",EDGE,"E187.top"),sQuery(id+"F23.wireOp",EDGE,"E187.right")])]});
            var Q4;
            Q4=makeQuery(id+"F22.boolean.opBoolean","COPY",EDGE,{"derivedFrom":makeQuery(id+"F22.opExtrude","SWEPT_EDGE",EDGE,{"disambiguationData":[OSD([sQuery(id+"F21.wireOp",EDGE,"E186.bottom"),sQuery(id+"F21.wireOp",EDGE,"E186.left")])]})});
            var Q5;
            Q5=makeQuery(id+"F22.boolean.opBoolean","COPY",EDGE,{"derivedFrom":makeQuery(id+"F22.opExtrude","SWEPT_EDGE",EDGE,{"disambiguationData":[OSD([sQuery(id+"F21.wireOp",EDGE,"E186.top"),sQuery(id+"F21.wireOp",EDGE,"E186.left")])]})});
            var Q6;
            Q6=makeQuery(id+"F24.opExtrude","SWEPT_EDGE",EDGE,{"disambiguationData":[OSD([sQuery(id+"F23.wireOp",EDGE,"E190.bottom"),sQuery(id+"F23.wireOp",EDGE,"E190.left")])]});
            var Q7;
            Q7=makeQuery(id+"F24.opExtrude","SWEPT_EDGE",EDGE,{"disambiguationData":[OSD([sQuery(id+"F23.wireOp",EDGE,"E188.top"),sQuery(id+"F23.wireOp",EDGE,"E188.left")])]});
            chamfer(context, id + "F25", {"entities" : qUnion([Q0, Q1, Q2, Q3, Q4, Q5, Q6, Q7]), "width" : 1 * mm, "tangentPropagation" : true});
        }
    });
